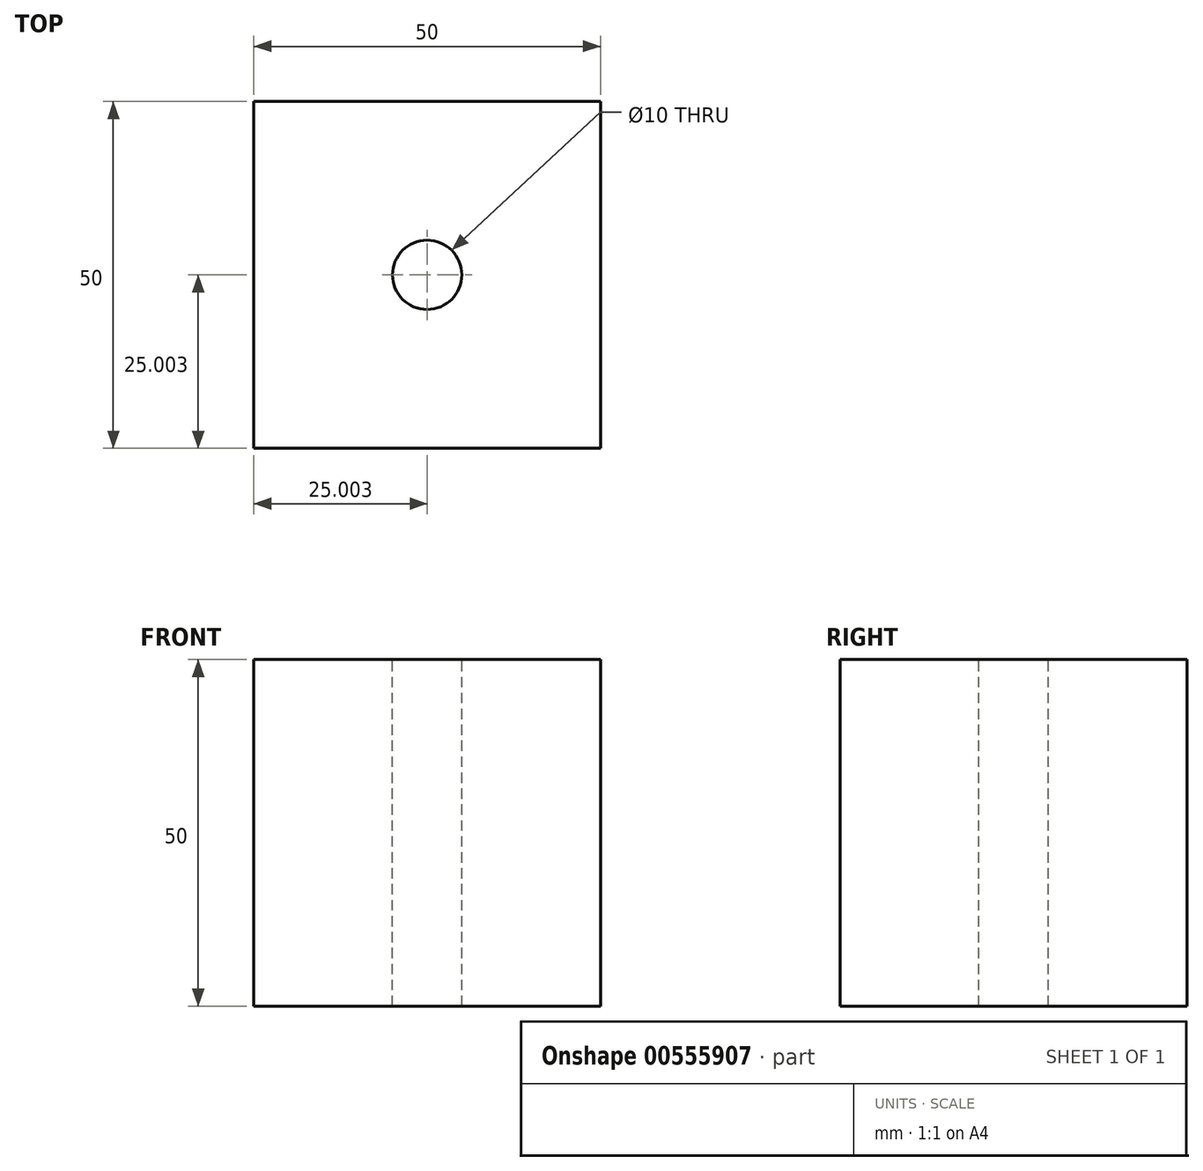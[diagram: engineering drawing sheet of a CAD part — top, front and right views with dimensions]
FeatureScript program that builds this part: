
annotation { "Feature Type Name" : "Feature", "Feature Type Description" : "" }
export const myFeature = defineFeature(function(context is Context, id is Id, definition is map)
    precondition{}
    {
        {
            var Q0;
            Q0=qCreatedBy(makeId("Top.planeOp"),FACE);
            var sketch = newSketch(context, id + "F0", { "sketchPlane" : qUnion([Q0])});
            skLineSegment(sketch, "E0.bottom", {"start": v(-75.27, 2) * mm, "end": v(-25.27, 2) * mm});
            skLineSegment(sketch, "E0.top", {"start": v(-75.27, -48) * mm, "end": v(-25.27, -48) * mm});
            skLineSegment(sketch, "E0.left", {"start": v(-75.27, 2) * mm, "end": v(-75.27, -48) * mm});
            skLineSegment(sketch, "E0.right", {"start": v(-25.27, 2) * mm, "end": v(-25.27, -48) * mm});
            skSolve(sketch);
        }
        {
            var Q0;
            Q0 = qSketchRegion(id + "F0", true);
            extrude(context, id + "F1", {"entities" : qUnion([Q0]), "depth" : 50 * mm, "offsetDistance" : 25 * mm});
        }
        {
            var Q0;
            Q0=makeQuery(id+"F1.opExtrude","CAP_FACE",FACE,{"disambiguationData":[OSD([sQuery(id+"F0.wireOp",EDGE,"E0.bottom"),sQuery(id+"F0.wireOp",EDGE,"E0.top"),sQuery(id+"F0.wireOp",EDGE,"E0.left"),sQuery(id+"F0.wireOp",EDGE,"E0.right")])],"isStart":false});
            var sketch = newSketch(context, id + "F2", { "sketchPlane" : qUnion([Q0])});
            skCircle(sketch, "E1", {"center": v(-50.27, -23) * mm, "radius": 5 * mm});
            skPoint(sketch, "E1.centerSnap0", {"position": v(-75.27, -23) * mm});
            skLineSegment(sketch, "E2", {"start": v(-25.27, -48) * mm, "end": v(-75.27, 2) * mm, "construction": true});
            skSolve(sketch);
        }
        {
            var Q0;
            Q0=makeQuery(id+"F2.imprint","IMPRINT",FACE,{"disambiguationData":[TD([[makeQuery(id+"F2.imprint","IMPRINT",EDGE,{"derivedFrom":sQuery(id+"F2.wireOp",EDGE,"E1")}),1.0]])]});
            var Q1;
            Q1=sQuery(id+"F2.wireOp",EDGE,"E1");
            extrude(context, id + "F3", {"entities" : qUnion([Q0]), "operationType" : NewBodyOperationType.REMOVE, "surfaceEntities" : qUnion([Q1]), "endBound" : BoundingType.UP_TO_NEXT, "oppositeDirection" : true, "depth" : 25 * mm, "offsetDistance" : 25 * mm});
        }
    });
